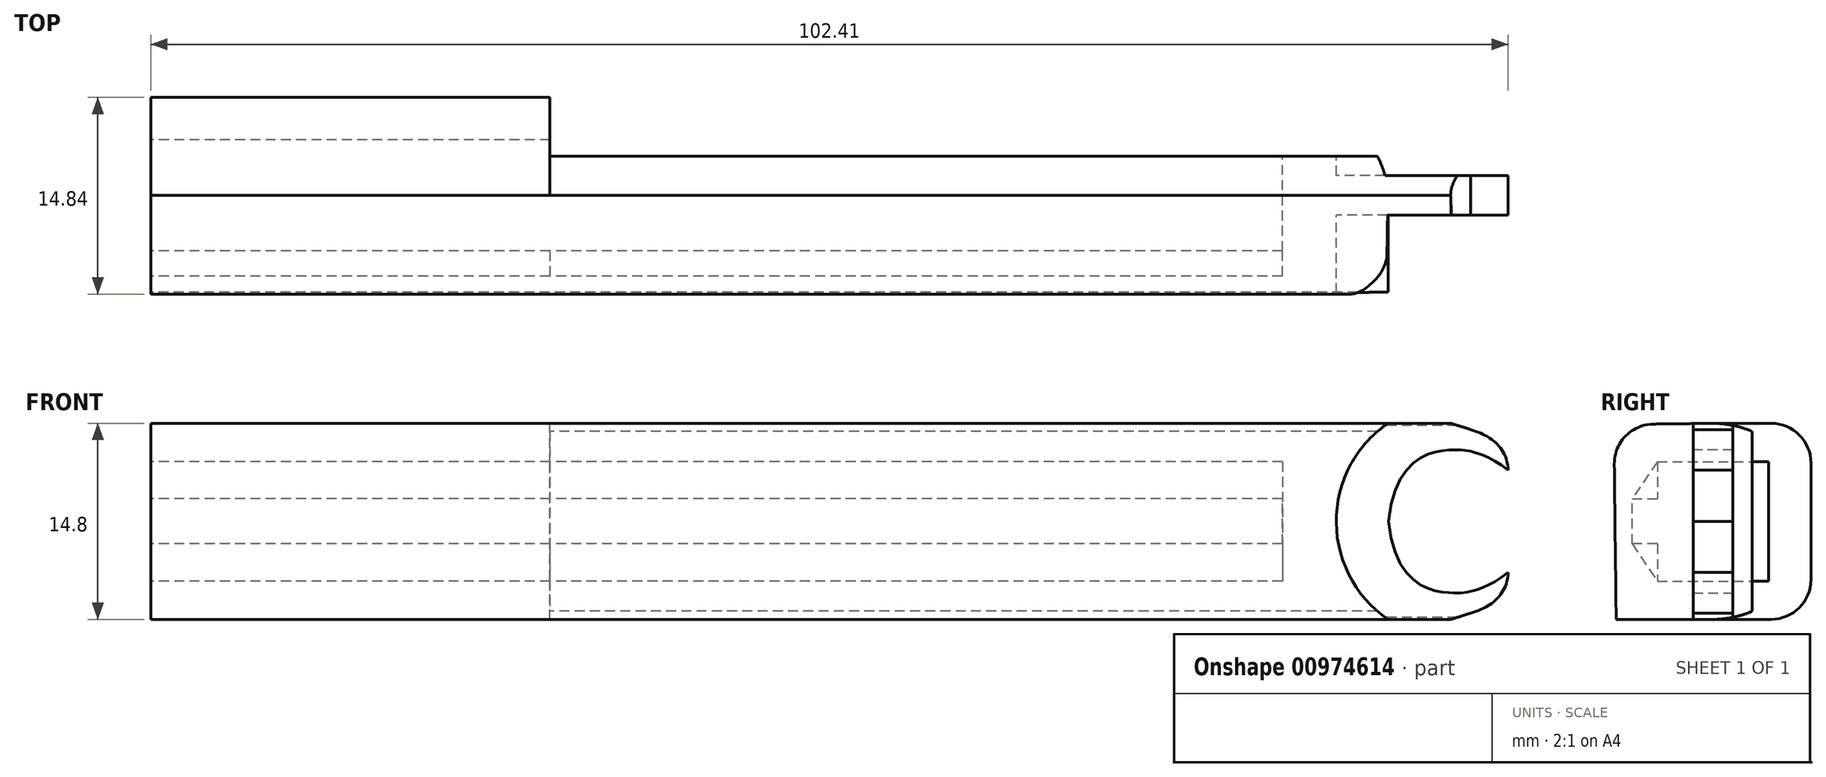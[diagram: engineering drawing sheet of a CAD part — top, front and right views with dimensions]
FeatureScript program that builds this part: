
annotation { "Feature Type Name" : "Feature", "Feature Type Description" : "" }
export const myFeature = defineFeature(function(context is Context, id is Id, definition is map)
    precondition{}
    {
        {
            var Q0;
            Q0=qCreatedBy(makeId("Right.planeOp"),FACE);
            var sketch = newSketch(context, id + "F0", { "sketchPlane" : qUnion([Q0])});
            skCircle(sketch, "E0", {"center": v(0, 0) * mm, "radius": 7.4 * mm});
            skLineSegment(sketch, "E1.bottom", {"start": v(-4.2, 4.5) * mm, "end": v(4.2, 4.5) * mm});
            skLineSegment(sketch, "E1.top", {"start": v(-4.2, -4.5) * mm, "end": v(4.2, -4.5) * mm});
            skLineSegment(sketch, "E1.left", {"start": v(-4.2, 4.5) * mm, "end": v(-4.2, -4.5) * mm});
            skLineSegment(sketch, "E1.right", {"start": v(4.2, 4.5) * mm, "end": v(4.2, -4.5) * mm});
            skLineSegment(sketch, "E2", {"start": v(0, 0) * mm, "end": v(-7.4, 0) * mm, "construction": true});
            skPoint(sketch, "E2.endSnap0", {"position": v(-4.2, 0) * mm});
            skLineSegment(sketch, "E3", {"start": v(-7.4, 0) * mm, "end": v(0, 0) * mm, "construction": true});
            skLineSegment(sketch, "E4", {"start": v(-4.2, -1.7) * mm, "end": v(-6.1, -1.7) * mm});
            skLineSegment(sketch, "E5", {"start": v(-6.1, -1.7) * mm, "end": v(-6.1, 1.7) * mm});
            skLineSegment(sketch, "E6", {"start": v(-6.1, 1.7) * mm, "end": v(-4.2, 1.7) * mm});
            skLineSegment(sketch, "E7", {"start": v(-4.2, 0) * mm, "end": v(-6.1, 0) * mm, "construction": true});
            skLineSegment(sketch, "E8", {"start": v(0, -7.4) * mm, "end": v(-7.3, -7.4) * mm});
            skLineSegment(sketch, "E9", {"start": v(-7.3, -7.4) * mm, "end": v(-7.48, 7.3) * mm});
            skLineSegment(sketch, "E10", {"start": v(-7.48, 7.3) * mm, "end": v(0, 7.4) * mm});
            skLineSegment(sketch, "E11", {"start": v(0, -7.4) * mm, "end": v(0, 7.4) * mm, "construction": true});
            skPoint(sketch, "E11.endSnap0", {"position": v(0, 4.5) * mm});
            skLineSegment(sketch, "E12", {"start": v(0, -7.4) * mm, "end": v(7.4, -7.4) * mm});
            skLineSegment(sketch, "E13", {"start": v(7.4, -7.4) * mm, "end": v(7.4, 7.4) * mm});
            skLineSegment(sketch, "E14", {"start": v(7.4, 7.4) * mm, "end": v(0, 7.4) * mm});
            skSolve(sketch);
        }
        {
            var Q0;
            Q0=makeQuery(id+"F0.imprint","IMPRINT",FACE,{"disambiguationData":[TD([[makeQuery(id+"F0.imprint","IMPRINT",EDGE,{"derivedFrom":sQuery(id+"F0.wireOp",EDGE,"E0")}),1.0]])]});
            var Q1;
            {var subQ0=sQuery(id+"F0.wireOp",EDGE,"E8");Q1=makeQuery(id+"F0.imprint","IMPRINT",FACE,{"disambiguationData":[TD([[makeQuery(id+"F0.imprint","IMPRINT",EDGE,{"derivedFrom":subQ0}),-1.0]])]});}
            var Q2;
            {var subQ0=sQuery(id+"F0.wireOp",EDGE,"E10");var subQ1=sQuery(id+"F0.wireOp",EDGE,"E0");var subQ2=makeQuery(id+"F0.imprint","INTERSECT",VERTEX,{"disambiguationData":[OD(1.0)],"derivedFrom":[subQ1,subQ0]});Q2=makeQuery(id+"F0.imprint","IMPRINT",FACE,{"disambiguationData":[TD([[makeQuery(id+"F0.imprint","IMPRINT",EDGE,{"disambiguationData":[TD([[subQ2,-1.0]])],"derivedFrom":subQ1}),-1.0]])]});}
            var Q3;
            {var subQ0=sQuery(id+"F0.wireOp",EDGE,"E12");Q3=makeQuery(id+"F0.imprint","IMPRINT",FACE,{"disambiguationData":[TD([[makeQuery(id+"F0.imprint","IMPRINT",EDGE,{"derivedFrom":subQ0}),1.0]])]});}
            var Q4;
            {var subQ0=sQuery(id+"F0.wireOp",EDGE,"E14");Q4=makeQuery(id+"F0.imprint","IMPRINT",FACE,{"disambiguationData":[TD([[makeQuery(id+"F0.imprint","IMPRINT",EDGE,{"derivedFrom":subQ0}),1.0]])]});}
            extrude(context, id + "F1", {"entities" : qUnion([Q0, Q1, Q2, Q3, Q4]), "depth" : 30.12 * mm, "offsetDistance" : 25 * mm});
        }
        {
            var Q0;
            Q0=makeQuery(id+"F1.opExtrude","CAP_FACE",FACE,{"disambiguationData":[OSD([sQuery(id+"F0.wireOp",EDGE,"E0"),sQuery(id+"F0.wireOp",EDGE,"E1.bottom"),sQuery(id+"F0.wireOp",EDGE,"E1.top"),sQuery(id+"F0.wireOp",EDGE,"E1.left"),sQuery(id+"F0.wireOp",EDGE,"E1.right"),sQuery(id+"F0.wireOp",EDGE,"E4"),sQuery(id+"F0.wireOp",EDGE,"E5"),sQuery(id+"F0.wireOp",EDGE,"E6")])],"isStart":false});
            var sketch = newSketch(context, id + "F2", { "sketchPlane" : qUnion([Q0])});
            skCircle(sketch, "E15", {"center": v(0, 0) * mm, "radius": 7.4 * mm});
            skLineSegment(sketch, "E16.bottom", {"start": v(-4.2, 4.5) * mm, "end": v(4.2, 4.5) * mm});
            skLineSegment(sketch, "E16.top", {"start": v(-4.2, -4.5) * mm, "end": v(4.2, -4.5) * mm});
            skLineSegment(sketch, "E16.left", {"start": v(-4.2, 4.5) * mm, "end": v(-4.2, -4.5) * mm});
            skLineSegment(sketch, "E16.right", {"start": v(4.2, 4.5) * mm, "end": v(4.2, -4.5) * mm});
            skLineSegment(sketch, "E17", {"start": v(0, 0) * mm, "end": v(-7.4, 0) * mm, "construction": true});
            skPoint(sketch, "E17.endSnap0", {"position": v(-4.2, 0) * mm});
            skLineSegment(sketch, "E18", {"start": v(-7.4, 0) * mm, "end": v(0, 0) * mm, "construction": true});
            skLineSegment(sketch, "E19", {"start": v(-4.2, -1.7) * mm, "end": v(-6.1, -1.7) * mm});
            skLineSegment(sketch, "E20", {"start": v(-6.1, -1.7) * mm, "end": v(-6.1, 1.7) * mm});
            skLineSegment(sketch, "E21", {"start": v(-6.1, 1.7) * mm, "end": v(-4.2, 1.7) * mm});
            skLineSegment(sketch, "E22", {"start": v(-4.2, 0) * mm, "end": v(-6.1, 0) * mm, "construction": true});
            skLineSegment(sketch, "E23", {"start": v(2.96, 6.77) * mm, "end": v(2.96, -6.77) * mm});
            skLineSegment(sketch, "E24", {"start": v(2.96, -6.77) * mm, "end": v(2.96, -4.5) * mm});
            skLineSegment(sketch, "E25", {"start": v(2.96, -4.5) * mm, "end": v(2.96, 4.5) * mm});
            skLineSegment(sketch, "E26", {"start": v(2.96, 4.5) * mm, "end": v(2.96, 6.77) * mm});
            skLineSegment(sketch, "E27", {"start": v(0, -7.4) * mm, "end": v(-7.3, -7.4) * mm});
            skLineSegment(sketch, "E28", {"start": v(-7.3, -7.4) * mm, "end": v(-7.48, 7.3) * mm});
            skLineSegment(sketch, "E29", {"start": v(-7.48, 7.3) * mm, "end": v(0, 7.4) * mm});
            skLineSegment(sketch, "E30", {"start": v(-4.2, 4.5) * mm, "end": v(-6.1, 1.7) * mm});
            skLineSegment(sketch, "E31", {"start": v(-6.1, -1.7) * mm, "end": v(-4.2, -4.5) * mm});
            skSolve(sketch);
        }
        {
            var Q0;
            {var subQ0=sQuery(id+"F2.wireOp",EDGE,"E29");var subQ1=sQuery(id+"F2.wireOp",EDGE,"E15");var subQ2=makeQuery(id+"F2.imprint","INTERSECT",VERTEX,{"disambiguationData":[OD(1.0)],"derivedFrom":[subQ1,subQ0]});Q0=makeQuery(id+"F2.imprint","IMPRINT",FACE,{"disambiguationData":[TD([[makeQuery(id+"F2.imprint","IMPRINT",EDGE,{"disambiguationData":[TD([[subQ2,-1.0]])],"derivedFrom":subQ1}),-1.0]])]});}
            var Q1;
            Q1=makeQuery(id+"F2.imprint","IMPRINT",FACE,{"disambiguationData":[TD([[makeQuery(id+"F2.imprint","IMPRINT",EDGE,{"derivedFrom":sQuery(id+"F2.wireOp",EDGE,"E20")}),1.0]])]});
            var Q2;
            {var subQ0=sQuery(id+"F2.wireOp",EDGE,"E27");Q2=makeQuery(id+"F2.imprint","IMPRINT",FACE,{"disambiguationData":[TD([[makeQuery(id+"F2.imprint","IMPRINT",EDGE,{"derivedFrom":subQ0}),-1.0]])]});}
            extrude(context, id + "F3", {"entities" : qUnion([Q0, Q1, Q2]), "operationType" : NewBodyOperationType.ADD, "depth" : 55.26 * mm, "offsetDistance" : 25 * mm});
        }
        {
            var Q0;
            Q0=makeQuery(id+"F3.opExtrude","CAP_FACE",FACE,{"disambiguationData":[OSD([sQuery(id+"F2.wireOp",EDGE,"E15"),sQuery(id+"F2.wireOp",EDGE,"E16.bottom"),sQuery(id+"F2.wireOp",EDGE,"E16.top"),sQuery(id+"F2.wireOp",EDGE,"E16.left"),sQuery(id+"F2.wireOp",EDGE,"E19"),sQuery(id+"F2.wireOp",EDGE,"E20"),sQuery(id+"F2.wireOp",EDGE,"E21"),sQuery(id+"F2.wireOp",EDGE,"E24"),sQuery(id+"F2.wireOp",EDGE,"E26")])],"isStart":false});
            var sketch = newSketch(context, id + "F4", { "sketchPlane" : qUnion([Q0])});
            skLineSegment(sketch, "E32", {"start": v(0, 7.4) * mm, "end": v(0, -7.4) * mm, "construction": true});
            skLineSegment(sketch, "E33", {"start": v(0, 7.4) * mm, "end": v(0, 0) * mm, "construction": true});
            skLineSegment(sketch, "E34.bottom", {"start": v(-8.13, -8.4) * mm, "end": v(8.13, -8.4) * mm});
            skLineSegment(sketch, "E34.top", {"start": v(-8.13, 8.4) * mm, "end": v(8.13, 8.4) * mm});
            skLineSegment(sketch, "E34.left", {"start": v(-8.13, -8.4) * mm, "end": v(-8.13, 8.4) * mm});
            skLineSegment(sketch, "E34.right", {"start": v(8.13, -8.4) * mm, "end": v(8.13, 8.4) * mm});
            skPoint(sketch, "E34.middle", {"position": v(0, 0) * mm});
            skLineSegment(sketch, "E35", {"start": v(2.96, 8.4) * mm, "end": v(2.96, -8.4) * mm});
            skSolve(sketch);
        }
        {
            var Q0;
            Q0=qCreatedBy(makeId("Front.planeOp"),FACE);
            var sketch = newSketch(context, id + "F5", { "sketchPlane" : qUnion([Q0])});
            skLineSegment(sketch, "E36.bottom", {"start": v(85.38, 7.4) * mm, "end": v(93.34, 7.4) * mm});
            skLineSegment(sketch, "E36.top", {"start": v(85.38, -7.4) * mm, "end": v(93.34, -7.4) * mm});
            skLineSegment(sketch, "E36.left", {"start": v(85.38, 7.4) * mm, "end": v(85.38, -7.4) * mm});
            skLineSegment(sketch, "E36.right", {"start": v(93.34, 7.4) * mm, "end": v(93.34, -7.4) * mm});
            skLineSegment(sketch, "E37", {"start": v(85.38, 0) * mm, "end": v(89.43, 0) * mm, "construction": true});
            skArc(sketch, "E38", {"start": v(93.34, 7.4) * mm, "mid": v(89.43, 0) * mm, "end": v(93.34, -7.4) * mm});
            skSolve(sketch);
        }
        {
            var Q0;
            Q0=makeQuery(id+"F5.imprint","IMPRINT",FACE,{"disambiguationData":[TD([[makeQuery(id+"F5.imprint","IMPRINT",EDGE,{"derivedFrom":sQuery(id+"F5.wireOp",EDGE,"E36.bottom")}),-1.0]])]});
            extrude(context, id + "F6", {"entities" : qUnion([Q0]), "operationType" : NewBodyOperationType.ADD, "endBound" : BoundingType.SYMMETRIC, "depth" : 15 * mm, "offsetDistance" : 25 * mm});
        }
        {
            var Q0;
            Q0=qCreatedBy(makeId("Front.planeOp"),FACE);
            var sketch = newSketch(context, id + "F7", { "sketchPlane" : qUnion([Q0])});
            skLineSegment(sketch, "E39", {"start": v(89.4, 0) * mm, "end": v(93.4, 0) * mm, "construction": true});
            skLineSegment(sketch, "E40", {"start": v(89.4, 0) * mm, "end": v(102.42, 0) * mm, "construction": true});
            skLineSegment(sketch, "E41", {"start": v(102.42, 3.6) * mm, "end": v(102.42, -3.6) * mm, "construction": true});
            skFitSpline(sketch, "E42", {"points": [v(102.42, -3.6) * mm, v(93.34, -7.4) * mm], "startDerivative": vector(0, -14.3) * mm, "endDerivative": vector(-4.13, -0.93) * mm});
            skFitSpline(sketch, "E43", {"points": [v(102.42, -3.85) * mm, v(99.44, -5.31) * mm, v(98.4, -5.4) * mm, v(93.4, 0) * mm], "startDerivative": vector(-12.26, -9.57) * mm, "endDerivative": vector(-3.08, 32.14) * mm});
            skFitSpline(sketch, "E44.MirrorCS", {"points": [v(102.42, 3.85) * mm, v(99.44, 5.31) * mm, v(98.4, 5.4) * mm, v(93.4, 0) * mm], "startDerivative": vector(-12.26, 9.57) * mm, "endDerivative": vector(-3.08, -32.14) * mm});
            skFitSpline(sketch, "E45.MirrorCS", {"points": [v(102.42, 3.6) * mm, v(93.34, 7.4) * mm], "startDerivative": vector(0, 14.3) * mm, "endDerivative": vector(-4.13, 0.93) * mm});
            skArc(sketch, "E46", {"start": v(93.34, 7.4) * mm, "mid": v(89.43, 0) * mm, "end": v(93.34, -7.4) * mm});
            skLineSegment(sketch, "E47", {"start": v(93.34, 7.4) * mm, "end": v(88.7, 7.4) * mm});
            skFitSpline(sketch, "E48", {"points": [v(99.56, 6.92) * mm, v(93.85, 8.1) * mm, v(88.7, 7.4) * mm], "startDerivative": vector(-11.23, 3.9) * mm, "endDerivative": vector(-10.46, -3.02) * mm});
            skFitSpline(sketch, "E49.MirrorCS", {"points": [v(99.56, -6.92) * mm, v(93.85, -8.1) * mm, v(88.7, -7.4) * mm], "startDerivative": vector(-11.23, -3.9) * mm, "endDerivative": vector(-10.46, 3.02) * mm});
            skLineSegment(sketch, "E50", {"start": v(93.34, -7.4) * mm, "end": v(88.7, -7.4) * mm});
            skSolve(sketch);
        }
        {
            var Q0;
            Q0 = qSketchRegion(id + "F7", true);
            extrude(context, id + "F8", {"entities" : qUnion([Q0]), "operationType" : NewBodyOperationType.ADD, "endBound" : BoundingType.SYMMETRIC, "depth" : 3 * mm, "offsetDistance" : 25 * mm});
        }
        {
            var Q0;
            {var subQ4=sQuery(id+"F4.wireOp",EDGE,"E34.left");Q0=makeQuery(id+"F4.imprint","IMPRINT",FACE,{"disambiguationData":[TD([[makeQuery(id+"F4.imprint","IMPRINT",EDGE,{"derivedFrom":subQ4}),-1.0]])]});}
            var Q1;
            {var subQ0=sQuery(id+"F4.wireOp",EDGE,"E34.right");Q1=makeQuery(id+"F4.imprint","IMPRINT",FACE,{"disambiguationData":[TD([[makeQuery(id+"F4.imprint","IMPRINT",EDGE,{"derivedFrom":subQ0}),1.0]])]});}
            extrude(context, id + "F9", {"entities" : qUnion([Q0, Q1]), "operationType" : NewBodyOperationType.REMOVE, "depth" : 13.7 * mm, "offsetDistance" : 25 * mm});
        }
        {
            var Q0;
            {var subQ0=sQuery(id+"F2.wireOp",EDGE,"E28");var subQ1=sQuery(id+"F2.wireOp",EDGE,"E27");Q0=makeQuery(id+"F9.boolean.opBoolean","MERGE",EDGE,{"derivedFrom":[makeQuery(id+"F3.boolean.opBoolean","MERGE",EDGE,{"derivedFrom":[makeQuery(id+"F1.opExtrude","SWEPT_EDGE",EDGE,{"disambiguationData":[OSD([sQuery(id+"F0.wireOp",EDGE,"E8"),sQuery(id+"F0.wireOp",EDGE,"E9")])]}),makeQuery(id+"F3.opExtrude","SWEPT_EDGE",EDGE,{"disambiguationData":[OSD([subQ1,subQ0])]})]})],"fromTools":[makeQuery(id+"F9.opExtrude","SWEPT_EDGE",EDGE,{"disambiguationData":[OSD([subQ1,subQ0])]})]});}
            var Q1;
            Q1=makeQuery(id+"F1.opExtrude","SWEPT_EDGE",EDGE,{"disambiguationData":[OSD([sQuery(id+"F0.wireOp",EDGE,"E13"),sQuery(id+"F0.wireOp",EDGE,"E14")])]});
            var Q2;
            Q2=makeQuery(id+"F1.opExtrude","SWEPT_EDGE",EDGE,{"disambiguationData":[OSD([sQuery(id+"F0.wireOp",EDGE,"E12"),sQuery(id+"F0.wireOp",EDGE,"E13")])]});
            var Q3;
            {var subQ0=sQuery(id+"F2.wireOp",EDGE,"E29");var subQ1=sQuery(id+"F2.wireOp",EDGE,"E28");Q3=makeQuery(id+"F9.boolean.opBoolean","MERGE",EDGE,{"derivedFrom":[makeQuery(id+"F3.boolean.opBoolean","MERGE",EDGE,{"derivedFrom":[makeQuery(id+"F1.opExtrude","SWEPT_EDGE",EDGE,{"disambiguationData":[OSD([sQuery(id+"F0.wireOp",EDGE,"E9"),sQuery(id+"F0.wireOp",EDGE,"E10")])]}),makeQuery(id+"F3.opExtrude","SWEPT_EDGE",EDGE,{"disambiguationData":[OSD([subQ1,subQ0])]})]})],"fromTools":[makeQuery(id+"F9.opExtrude","SWEPT_EDGE",EDGE,{"disambiguationData":[OSD([subQ1,subQ0])]})]});}
            fillet(context, id + "F10", {"entities" : qUnion([Q0, Q1, Q2, Q3]), "radius" : 3 * mm, "tangentPropagation" : true, "allowEdgeOverflow" : false});
        }
    });
